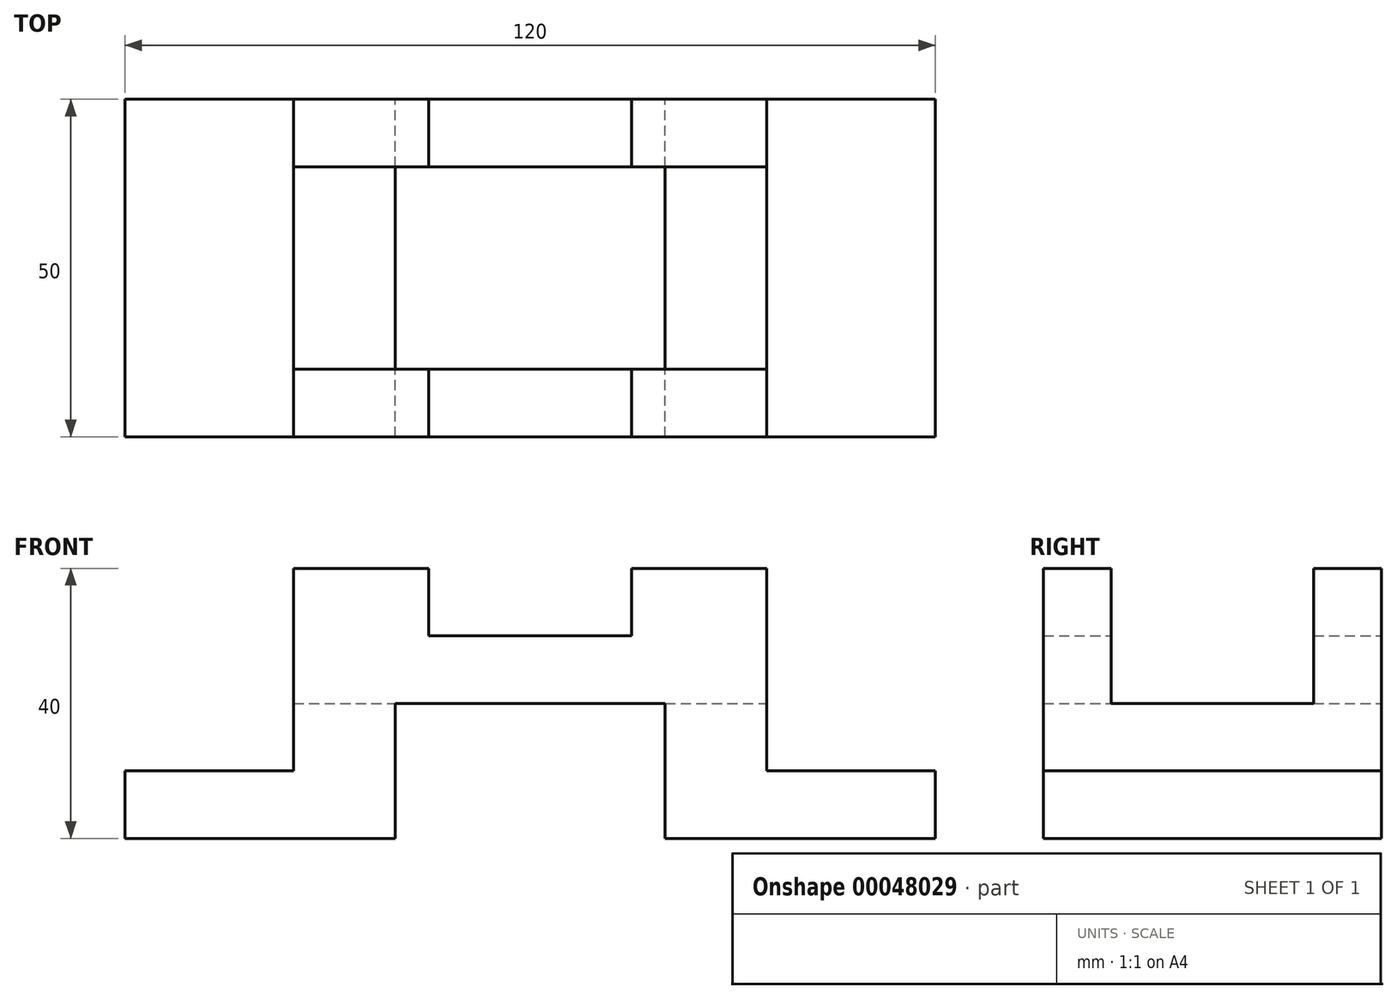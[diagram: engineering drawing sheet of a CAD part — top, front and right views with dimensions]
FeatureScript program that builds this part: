
annotation { "Feature Type Name" : "Feature", "Feature Type Description" : "" }
export const myFeature = defineFeature(function(context is Context, id is Id, definition is map)
    precondition{}
    {
        {
            var Q0;
            Q0=qCreatedBy(makeId("Front.planeOp"),FACE);
            var sketch = newSketch(context, id + "F0", { "sketchPlane" : qUnion([Q0])});
            skLineSegment(sketch, "E0", {"start": v(0, 0) * mm, "end": v(0, 10) * mm});
            skLineSegment(sketch, "E1", {"start": v(0, 10) * mm, "end": v(25, 10) * mm});
            skLineSegment(sketch, "E2", {"start": v(25, 10) * mm, "end": v(25, 40) * mm});
            skLineSegment(sketch, "E3", {"start": v(25, 40) * mm, "end": v(45, 40) * mm});
            skLineSegment(sketch, "E4", {"start": v(45, 40) * mm, "end": v(45, 30) * mm});
            skLineSegment(sketch, "E5", {"start": v(45, 30) * mm, "end": v(75, 30) * mm});
            skLineSegment(sketch, "E6", {"start": v(75, 30) * mm, "end": v(75, 40) * mm});
            skLineSegment(sketch, "E7", {"start": v(75, 40) * mm, "end": v(95, 40) * mm});
            skLineSegment(sketch, "E8", {"start": v(95, 40) * mm, "end": v(95, 10) * mm});
            skLineSegment(sketch, "E9", {"start": v(95, 10) * mm, "end": v(120, 10) * mm});
            skLineSegment(sketch, "E10", {"start": v(120, 10) * mm, "end": v(120, 0) * mm});
            skLineSegment(sketch, "E11", {"start": v(120, 0) * mm, "end": v(80, 0) * mm});
            skLineSegment(sketch, "E12", {"start": v(80, 0) * mm, "end": v(80, 20) * mm});
            skLineSegment(sketch, "E13", {"start": v(80, 20) * mm, "end": v(40, 20) * mm});
            skLineSegment(sketch, "E14", {"start": v(40, 20) * mm, "end": v(40, 0) * mm});
            skLineSegment(sketch, "E15", {"start": v(40, 0) * mm, "end": v(0, 0) * mm});
            skSolve(sketch);
        }
        {
            var Q0;
            Q0=makeQuery(id+"F0.imprint","IMPRINT",FACE,{"disambiguationData":[TD([[makeQuery(id+"F0.imprint","IMPRINT",EDGE,{"derivedFrom":sQuery(id+"F0.wireOp",EDGE,"E0")}),-1.0]])]});
            extrude(context, id + "F1", {"entities" : qUnion([Q0]), "endBound" : BoundingType.SYMMETRIC, "depth" : 50 * mm});
        }
        {
            var Q0;
            Q0=makeQuery(id+"F1.opExtrude","SWEPT_FACE",FACE,{"disambiguationData":[OSD([sQuery(id+"F0.wireOp",EDGE,"E8")])]});
            var sketch = newSketch(context, id + "F2", { "sketchPlane" : qUnion([Q0])});
            skLineSegment(sketch, "E16", {"start": v(-15, 40) * mm, "end": v(-15, 20) * mm});
            skLineSegment(sketch, "E17", {"start": v(-15, 20) * mm, "end": v(15, 20) * mm});
            skLineSegment(sketch, "E18", {"start": v(15, 20) * mm, "end": v(15, 40) * mm});
            skSolve(sketch);
        }
        {
            var Q0;
            {var subQ2=sQuery(id+"F2.wireOp",EDGE,"E16");Q0=makeQuery(id+"F2.imprint","IMPRINT",FACE,{"disambiguationData":[TD([[makeQuery(id+"F2.imprint","IMPRINT",EDGE,{"derivedFrom":subQ2}),1.0]])]});}
            extrude(context, id + "F3", {"entities" : qUnion([Q0]), "operationType" : NewBodyOperationType.REMOVE, "endBound" : BoundingType.THROUGH_ALL, "oppositeDirection" : true, "depth" : 25 * mm});
        }
    });
